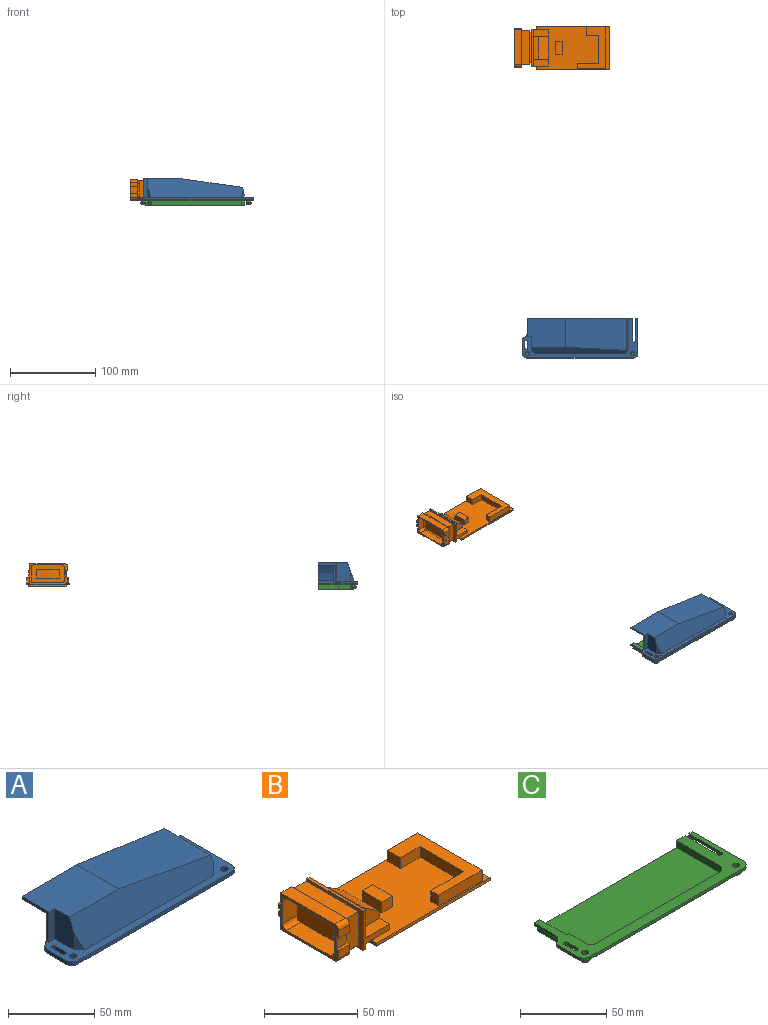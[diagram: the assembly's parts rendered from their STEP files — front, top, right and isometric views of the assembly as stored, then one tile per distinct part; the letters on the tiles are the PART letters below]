
ASSEMBLY  parts=3 mates=2
PART A: 68 faces, bbox 135.6x46.8x24 mm
  f0: plane 135.6x46.8mm, normal (0,0,1), area 1178.6mm2, adj f1,f4,f10,f13,f14,f29,f30,f31
  f1: plane 3x2.6mm, normal (0,1,0), area 7.8mm2, adj f0,f2,f56,f59
  f2: plane 135.6x46.8mm, normal (0,0,-1), area 690.3mm2, adj f1,f13,f14,f24,f25,f26,f27,f28
  f3: plane 119.6x44.8mm, normal (0,0,-1), area 500.9mm2, adj f5,f6,f13,f19,f20,f21,f22,f23
  f4: plane 21.4x15.83mm, normal (-1,0,0), area 320.8mm2, adj f0,f30,f33,f39,f44
  f5: plane 22x2.1mm, normal (0,1,0), area 45.5mm2, adj f3,f6,f9,f11,f12,f22,f40,f42
  f6: plane 21.5x20.4mm, normal (1,0,0), area 97.4mm2, adj f3,f5,f7,f9,f13,f46,f67
  f7: plane 16.1x1.8mm, normal (0,0,-1), area 28.9mm2, adj f6,f13,f43,f67
  f8: plane 20.1x2.9mm, normal (0,0,-1), area 58.4mm2, adj f10,f13,f43,f47,f66
  f9: plane 21.5x1.85mm, normal (0,0,-1), area 39.8mm2, adj f5,f6,f13,f40
  f10: plane 22x21.4mm, normal (-1,0,0), area 80.9mm2, adj f0,f8,f13,f33,f44,f66
  f11: plane 22x15.5mm, normal (1,0,0), area 314.3mm2, adj f5,f12,f18,f32,f38,f42,f48
  f12: plane 114x42mm, normal (0,0,-1), area 336.6mm2, adj f5,f11,f13,f15,f16,f17,f18,f19
  f13: plane 123.6x24mm, normal (0,1,0), area 271.4mm2, adj f0,f2,f3,f6,f7,f8,f9,f10
  f14: plane 125.6x2.6mm, normal (0,-1,0), area 326.6mm2, adj f0,f2,f54,f55
  f15: plane 37x2.88mm, normal (-1,0,0), area 106.6mm2, adj f12,f13,f16,f36
  f16: plane 7.91x3mm, normal (-0.71,0.71,0), area 22.5mm2, adj f12,f15,f17,f36,f38
  f17: plane 104x2.6mm, normal (0,1,0), area 270.4mm2, adj f12,f16,f18,f38
  f18: plane 10.84x3mm, normal (0.71,0.71,0), area 28.5mm2, adj f11,f12,f17,f38
  f19: plane 105.66x1.6mm, normal (0,-1,0), area 169.1mm2, adj f3,f12,f20,f23
  f20: plane 4.17x4.17mm, normal (0.71,-0.71,0), area 9.4mm2, adj f3,f12,f19,f21
  f21: plane 37.83x1.6mm, normal (1,0,0), area 60.5mm2, adj f3,f12,f13,f20
  f22: plane 16.33x1.6mm, normal (-1,0,0), area 26.1mm2, adj f3,f5,f12,f23
  f23: plane 4.17x4.17mm, normal (-0.71,-0.71,0), area 9.4mm2, adj f3,f12,f19,f22
  f24: plane 5.81x5.81mm, normal (0.71,0.71,0), area 13.2mm2, adj f2,f3,f25,f28
  f25: plane 18.89x1.6mm, normal (1,0,0), area 30.2mm2, adj f2,f3,f24,f47
  f26: plane 38.99x1.6mm, normal (-1,0,0), area 62.4mm2, adj f2,f3,f13,f27
  f27: plane 5.81x5.81mm, normal (-0.71,0.71,0), area 13.2mm2, adj f2,f3,f26,f28
  f28: plane 107.98x1.6mm, normal (0,1,0), area 172.8mm2, adj f2,f3,f24,f27
  f29: plane 37.83x0.01mm, normal (1,0,0), area 0.4mm2, adj f0,f13,f31,f37
  f30: plane 11.46x4.17mm, normal (-0.71,-0.71,0), area 33.8mm2, adj f0,f4,f39
  f31: plane 7.24x4.17mm, normal (0.71,-0.71,0), area 21.4mm2, adj f0,f29,f37,f39
  f32: plane 38x32.94mm, normal (0,0,-1), area 1212.6mm2, adj f11,f13,f34,f38,f41,f48,f49
  f33: plane 44.8x34.21mm, normal (0,0,1), area 1474mm2, adj f4,f10,f13,f35,f39,f44
  f34: plane 70.03x36.52mm, normal (-0.14,0,-0.99), area 2456mm2, adj f13,f32,f36,f38
  f35: plane 71.59x37.87mm, normal (0.14,0,0.99), area 2605.7mm2, adj f13,f33,f37,f39
  f36: plane 38.07x9.28mm, normal (-0.98,0,-0.21), area 354.9mm2, adj f13,f15,f16,f34,f38
  f37: plane 39.37x11.33mm, normal (0.98,0,0.21), area 447.1mm2, adj f13,f29,f31,f35,f39
  f38: plane 108.93x19.4mm, normal (0,0.94,-0.34), area 1852.1mm2, adj f11,f16,f17,f18,f32,f34,f36
  f39: plane 112.46x21.4mm, normal (0,-0.94,0.34), area 2131.1mm2, adj f0,f4,f30,f31,f33,f35,f37
  f40: plane 21.5x2mm, normal (-1,0,0), area 43mm2, adj f5,f9,f13,f42
  f41: plane 19.68x2mm, normal (1,0,0), area 39.4mm2, adj f13,f32,f42,f49
  f42: plane 23.5x2mm, normal (0,0,-1), area 44.4mm2, adj f5,f11,f13,f40,f41,f48,f49
  f43: plane 20.11x1.51mm, normal (-1,0,0), area 30.2mm2, adj f7,f8,f13,f45,f47
  f44: plane 21.4x4.8mm, normal (0,-1,0), area 102.7mm2, adj f0,f4,f10,f33
  f45: plane 18.91x4.01mm, normal (-1,0,0), area 38.7mm2, adj f3,f43,f46,f47,f67
  f46: plane 16.9x1.8mm, normal (0,1,0), area 30.4mm2, adj f3,f6,f45,f67
  f47: plane 22x2.9mm, normal (0,1,0), area 62.4mm2, adj f2,f3,f8,f25,f43,f45,f66
  f48: plane 2x0.29mm, normal (0.71,-0.71,0), area 0.8mm2, adj f11,f32,f42,f49
  f49: cylinder r=5mm len=3.54mm, axis (0,0,-1), area 7.9mm2, adj f32,f41,f42,f48
  f50: cylinder r=5mm len=2.6mm, axis (0,0,1), area 4.6mm2, adj f0,f2,f51,f66
  f51: plane 2.6x1mm, normal (-0.5,0.87,0), area 3mm2, adj f0,f2,f50,f52
  f52: cylinder r=5mm len=4.33mm, axis (0,0,1), area 13.6mm2, adj f0,f2,f51,f53
  f53: plane 15.11x2.6mm, normal (-1,0,0), area 39.3mm2, adj f0,f2,f52,f54
  f54: cylinder r=5mm len=5mm, axis (0,0,1), area 20.4mm2, adj f0,f2,f14,f53
  f55: cylinder r=5mm len=5mm, axis (0,0,1), area 20.4mm2, adj f0,f2,f14,f56
  f56: plane 41.8x2.6mm, normal (1,0,0), area 108.7mm2, adj f0,f1,f2,f55
  f57: cylinder r=2.25mm len=4.5mm, axis (0,0,1), area 36.8mm2, adj f0,f2
  f58: cylinder r=2.25mm len=4.5mm, axis (0,0,1), area 36.8mm2, adj f0,f2
  f59: plane 27x2.6mm, normal (-1,0,0), area 70.2mm2, adj f0,f1,f2,f60
  f60: cylinder r=1.5mm len=3mm, axis (0,0,-1), area 12.3mm2, adj f0,f2,f59,f61
  f61: plane 27x2.6mm, normal (1,0,0), area 70.2mm2, adj f0,f2,f13,f60
  f62: cylinder r=1.5mm len=3mm, axis (0,0,-1), area 12.3mm2, adj f0,f2,f63,f65
  f63: plane 8x2.6mm, normal (1,0,0), area 20.8mm2, adj f0,f2,f62,f64
  f64: cylinder r=1.5mm len=3mm, axis (0,0,-1), area 12.3mm2, adj f0,f2,f63,f65
  f65: plane 8x2.6mm, normal (-1,0,0), area 20.8mm2, adj f0,f2,f62,f64
  f66: cylinder r=1.5mm len=22mm, axis (0,0,1), area 3.5mm2, adj f0,f2,f8,f10,f47,f50
  f67: cylinder r=2mm len=2mm, axis (-1,0,0), area 5.6mm2, adj f6,f7,f45,f46
PART B: 97 faces, bbox 112.3x51x27.4 mm
  f0: plane 5x1.5mm, normal (1,0,0), area 7.5mm2, adj f7,f87,f89,f94
  f1: plane 78x2.4mm, normal (0,1,0), area 119.7mm2, adj f85,f88,f89,f94,f95,f96
  f2: plane 70x1.5mm, normal (0,-1,0), area 105mm2, adj f3,f85,f89,f94
  f3: plane 14x1.5mm, normal (1,0,0), area 21mm2, adj f2,f4,f89,f94
  f4: plane 70x1.5mm, normal (0,1,0), area 105mm2, adj f3,f86,f89,f94
  f5: plane 70x1.5mm, normal (0,-1,0), area 105mm2, adj f6,f86,f89,f94
  f6: plane 14x1.5mm, normal (1,0,0), area 21mm2, adj f5,f7,f89,f94
  f7: plane 70x1.5mm, normal (0,1,0), area 105mm2, adj f0,f6,f89,f94
  f8: plane 86x2mm, normal (0,1,0), area 172mm2, adj f15,f16,f17,f89
  f9: plane 86x2mm, normal (0,-1,0), area 172mm2, adj f15,f16,f17,f89
  f10: plane 8.3x8mm, normal (0,-1,0), area 66.4mm2, adj f61,f62,f75,f77
  f11: plane 8.3x8mm, normal (0,1,0), area 66.4mm2, adj f55,f61,f62,f72
  f12: plane 8.3x2mm, normal (0,1,0), area 16.6mm2, adj f61,f62,f71,f73
  f13: plane 43x8mm, normal (1,0,0), area 272mm2, adj f15,f33,f36,f37,f39,f40,f41,f42
  f14: plane 43x18.5mm, normal (1,0,0), area 444.5mm2, adj f33,f34,f36,f37,f38,f40,f41,f42
  f15: plane 86x51mm, normal (0,0,1), area 2972mm2, adj f8,f9,f13,f16,f17,f18,f19,f20
  f16: plane 51x2mm, normal (-1,0,0), area 102mm2, adj f8,f9,f15,f32,f89
  f17: plane 51x2mm, normal (1,0,0), area 102mm2, adj f8,f9,f15,f89
  f18: plane 33x7mm, normal (-1,0,0), area 231mm2, adj f15,f19,f25,f26
  f19: plane 15x7mm, normal (0,-1,0), area 105mm2, adj f15,f18,f20,f26
  f20: plane 10x7mm, normal (-1,0,0), area 70mm2, adj f15,f19,f21,f26
  f21: plane 23x7mm, normal (0,1,0), area 161mm2, adj f15,f20,f22,f26
  f22: plane 49x7mm, normal (1,0,0), area 343mm2, adj f15,f21,f23,f26
  f23: plane 33x7mm, normal (0,-1,0), area 231mm2, adj f15,f22,f24,f26
  f24: plane 7x6mm, normal (-1,0,0), area 42mm2, adj f15,f23,f25,f26
  f25: plane 25x7mm, normal (0,1,0), area 175mm2, adj f15,f18,f24,f26
  f26: plane 49x33mm, normal (0,0,1), area 692mm2, adj f18,f19,f20,f21,f22,f23,f24,f25
  f27: plane 8x7mm, normal (0,1,0), area 56mm2, adj f15,f28,f30,f31
  f28: plane 15x7mm, normal (1,0,0), area 105mm2, adj f15,f27,f29,f31
  f29: plane 8x7mm, normal (0,-1,0), area 56mm2, adj f15,f28,f30,f31
  f30: plane 15x7mm, normal (-1,0,0), area 105mm2, adj f15,f27,f29,f31
  f31: plane 15x8mm, normal (0,0,1), area 120mm2, adj f27,f28,f29,f30
  f32: plane 43x4.8mm, normal (0,0,-1), area 206.4mm2, adj f16,f36,f37,f44
  f33: plane 18.25x8mm, normal (0,0,1), area 146mm2, adj f13,f14,f36,f40
  f34: plane 43x1.75mm, normal (0,0,1), area 75.3mm2, adj f14,f35,f36,f37
  f35: plane 43x26mm, normal (-1,0,0), area 437.4mm2, adj f34,f36,f37,f43,f45,f46,f47,f48
  f36: plane 26x20mm, normal (0,1,0), area 107.2mm2, adj f13,f14,f15,f32,f33,f34,f35,f43
  f37: plane 26x20mm, normal (0,-1,0), area 107.2mm2, adj f13,f14,f15,f32,f34,f35,f41,f43
  f38: plane 27x6mm, normal (0,0,1), area 162mm2, adj f14,f39,f40,f42
  f39: plane 27x12.25mm, normal (0.57,0,0.82), area 402.6mm2, adj f13,f38,f40,f42
  f40: plane 18.25x13mm, normal (0,1,0), area 185.2mm2, adj f13,f14,f33,f38,f39
  f41: plane 18.25x8mm, normal (0,0,1), area 146mm2, adj f13,f14,f37,f42
  f42: plane 18.25x13mm, normal (0,-1,0), area 185.2mm2, adj f13,f14,f38,f39,f41
  f43: plane 43x1.2mm, normal (0,0,-1), area 51.6mm2, adj f35,f36,f37,f44
  f44: plane 43x4mm, normal (1,0,0), area 172mm2, adj f32,f36,f37,f43
  f45: plane 32x2mm, normal (0,0,1), area 64mm2, adj f35,f53,f90,f93
  f46: plane 15x2mm, normal (0,1,0), area 30mm2, adj f35,f53,f90,f91
  f47: plane 32x2mm, normal (0,0,-1), area 64mm2, adj f35,f53,f91,f92
  f48: plane 15x2mm, normal (0,-1,0), area 30mm2, adj f35,f53,f92,f93
  f49: plane 40x10mm, normal (0,0,1), area 400mm2, adj f50,f52,f53,f62
  f50: plane 22x10mm, normal (0,1,0), area 220mm2, adj f49,f51,f53,f62
  f51: plane 40x10mm, normal (0,0,-1), area 400mm2, adj f50,f52,f53,f62
  f52: plane 22x10mm, normal (0,-1,0), area 220mm2, adj f49,f51,f53,f62
  f53: plane 40x22mm, normal (1,0,0), area 199.4mm2, adj f45,f46,f47,f48,f49,f50,f51,f52
  f54: plane 8.3x8mm, normal (0,1,0), area 66.4mm2, adj f60,f61,f62,f69
  f55: plane 41x8.3mm, normal (0,0,-1), area 340.3mm2, adj f11,f61,f62,f79
  f56: plane 33x11mm, normal (0,0,-1), area 363mm2, adj f61,f63,f81,f84
  f57: plane 15x11mm, normal (0,1,0), area 165mm2, adj f61,f63,f81,f82
  f58: plane 33x11mm, normal (0,0,1), area 363mm2, adj f61,f63,f82,f83
  f59: plane 15x11mm, normal (0,-1,0), area 165mm2, adj f61,f63,f83,f84
  f60: plane 41x8.3mm, normal (0,0,1), area 340.3mm2, adj f54,f61,f62,f80
  f61: plane 46x24mm, normal (-1,0,0), area 236.9mm2, adj f10,f11,f12,f54,f55,f56,f57,f58
  f62: plane 46x24mm, normal (1,0,0), area 168.1mm2, adj f10,f11,f12,f49,f50,f51,f52,f54
  f63: plane 39x21mm, normal (-1,0,0), area 541.3mm2, adj f56,f57,f58,f59,f65,f66,f67,f68
  f64: plane 27x10mm, normal (-1,0,0), area 270mm2, adj f65,f66,f67,f68
  f65: plane 10x5.7mm, normal (0,-1,0), area 57mm2, adj f63,f64,f66,f68
  f66: plane 27x5.7mm, normal (0,0,1), area 153.9mm2, adj f63,f64,f65,f67
  f67: plane 10x5.7mm, normal (0,1,0), area 57mm2, adj f63,f64,f66,f68
  f68: plane 27x5.7mm, normal (0,0,-1), area 153.9mm2, adj f63,f64,f65,f67
  f69: plane 8.3x2mm, normal (0,0,1), area 16.6mm2, adj f54,f61,f62,f70
  f70: plane 8.3x3mm, normal (0,1,0), area 24.9mm2, adj f61,f62,f69,f71
  f71: plane 8.3x2mm, normal (0,0,-1), area 16.6mm2, adj f12,f61,f62,f70
  f72: plane 8.3x2mm, normal (0,0,-1), area 16.6mm2, adj f11,f61,f62,f74
  f73: plane 8.3x2mm, normal (0,0,1), area 16.6mm2, adj f12,f61,f62,f74
  f74: plane 8.3x3mm, normal (0,1,0), area 24.9mm2, adj f61,f62,f72,f73
  f75: plane 8.3x2mm, normal (0,0,-1), area 16.6mm2, adj f10,f61,f62,f76
  f76: plane 8.3x5mm, normal (0,-1,0), area 41.5mm2, adj f61,f62,f75,f80
  f77: plane 8.3x2mm, normal (0,0,1), area 16.6mm2, adj f10,f61,f62,f78
  f78: plane 8.3x5mm, normal (0,-1,0), area 41.5mm2, adj f61,f62,f77,f79
  f79: cylinder r=3mm len=8.3mm, axis (-1,0,0), area 39.1mm2, adj f55,f61,f62,f78
  f80: cylinder r=3mm len=8.3mm, axis (-1,0,0), area 39.1mm2, adj f60,f61,f62,f76
  f81: cylinder r=3mm len=11mm, axis (-1,0,0), area 51.8mm2, adj f56,f57,f61,f63
  f82: cylinder r=3mm len=11mm, axis (1,0,0), area 51.8mm2, adj f57,f58,f61,f63
  f83: cylinder r=3mm len=11mm, axis (-1,0,0), area 51.8mm2, adj f58,f59,f61,f63
  f84: cylinder r=3mm len=11mm, axis (1,0,0), area 51.8mm2, adj f56,f59,f61,f63
  f85: plane 5x1.5mm, normal (1,0,0), area 7.5mm2, adj f1,f2,f89,f94
  f86: plane 7x1.5mm, normal (1,0,0), area 10.5mm2, adj f4,f5,f89,f94
  f87: plane 78x2.4mm, normal (0,-1,0), area 119.7mm2, adj f0,f88,f89,f94,f95,f96
  f88: plane 45x2.4mm, normal (-1,0,0), area 108mm2, adj f1,f87,f89,f95
  f89: plane 86x51mm, normal (0,0,-1), area 2836mm2, adj f0,f1,f2,f3,f4,f5,f6,f7
  f90: cylinder r=2mm len=2mm, axis (-1,0,0), area 6.3mm2, adj f35,f45,f46,f53
  f91: cylinder r=2mm len=2mm, axis (1,0,0), area 6.3mm2, adj f35,f46,f47,f53
  f92: cylinder r=2mm len=2mm, axis (-1,0,0), area 6.3mm2, adj f35,f47,f48,f53
  f93: cylinder r=2mm len=2mm, axis (1,0,0), area 6.3mm2, adj f35,f45,f48,f53
  f94: plane 75x45mm, normal (0,0,-1), area 1415mm2, adj f0,f1,f2,f3,f4,f5,f6,f7
  f95: plane 45x3mm, normal (0,0,-1), area 135mm2, adj f1,f87,f88,f96
  f96: plane 45x0.9mm, normal (1,0,0), area 40.5mm2, adj f1,f87,f94,f95
PART C: 46 faces, bbox 135.6x46.8x7 mm
  f0: plane 135.6x46.8mm, normal (0,0,-1), area 1213.2mm2, adj f2,f3,f4,f5,f13,f14,f15,f16
  f1: plane 135.6x46.8mm, normal (0,0,1), area 1628.2mm2, adj f2,f3,f4,f5,f6,f7,f8,f9
  f2: plane 3x2mm, normal (0,1,0), area 6mm2, adj f0,f1,f23,f27
  f3: plane 17.45x2mm, normal (-1,0,0), area 34.9mm2, adj f0,f1,f4,f32
  f4: plane 123.6x7mm, normal (0,1,0), area 267.2mm2, adj f0,f1,f3,f10,f12,f13,f14,f20
  f5: plane 125.6x2mm, normal (0,-1,0), area 251.2mm2, adj f0,f1,f33,f35
  f6: plane 15.5x5mm, normal (1,0,0), area 77.5mm2, adj f1,f7,f11,f20
  f7: plane 5x3mm, normal (0.71,0.71,0), area 21.2mm2, adj f1,f6,f8,f20
  f8: plane 104x5mm, normal (0,1,0), area 520mm2, adj f1,f7,f9,f20
  f9: plane 5x3mm, normal (-0.71,0.71,0), area 21.2mm2, adj f1,f8,f10,f20
  f10: plane 37x5mm, normal (-1,0,0), area 185mm2, adj f1,f4,f9,f20
  f11: plane 5x2mm, normal (0,1,0), area 10mm2, adj f1,f6,f12,f20
  f12: plane 21.5x5mm, normal (1,0,0), area 107.5mm2, adj f1,f4,f11,f20
  f13: plane 23.5x5mm, normal (-1,0,0), area 117.5mm2, adj f0,f4,f19,f21
  f14: plane 37.83x5mm, normal (1,0,0), area 189.1mm2, adj f0,f4,f15,f21
  f15: plane 5x4.17mm, normal (0.71,-0.71,0), area 29.5mm2, adj f0,f14,f16,f21
  f16: plane 105.66x5mm, normal (0,-1,0), area 528.3mm2, adj f0,f15,f17,f21
  f17: plane 5x4.17mm, normal (-0.71,-0.71,0), area 29.5mm2, adj f0,f16,f18,f21
  f18: plane 14.33x5mm, normal (-1,0,0), area 71.6mm2, adj f0,f17,f19,f21
  f19: plane 5x2mm, normal (0,-1,0), area 10mm2, adj f0,f13,f18,f21
  f20: plane 112x40mm, normal (0,0,1), area 4434mm2, adj f4,f6,f7,f8,f9,f10,f11,f12
  f21: plane 116x42mm, normal (0,0,-1), area 4817.6mm2, adj f4,f13,f14,f15,f16,f17,f18,f19
  f22: plane 15.11x2mm, normal (-1,0,0), area 30.2mm2, adj f0,f1,f33,f34
  f23: plane 41.8x2mm, normal (1,0,0), area 83.6mm2, adj f0,f1,f2,f35
  f24: plane 8x2mm, normal (-1,0,0), area 16mm2, adj f0,f1,f28,f29
  f25: plane 8x2mm, normal (1,0,0), area 16mm2, adj f0,f1,f28,f29
  f26: plane 27x2mm, normal (1,0,0), area 54mm2, adj f0,f1,f4,f30
  f27: plane 27x2mm, normal (-1,0,0), area 54mm2, adj f0,f1,f2,f30
  f28: cylinder r=1.5mm len=3mm, axis (0,0,1), area 9.4mm2, adj f0,f1,f24,f25
  f29: cylinder r=1.5mm len=3mm, axis (0,0,1), area 9.4mm2, adj f0,f1,f24,f25
  f30: cylinder r=1.5mm len=3mm, axis (0,0,-1), area 9.4mm2, adj f0,f1,f26,f27
  f31: plane 2x1mm, normal (-0.5,0.87,0), area 2.3mm2, adj f0,f1,f32,f34
  f32: cylinder r=5mm len=4.33mm, axis (0,0,-1), area 10.5mm2, adj f0,f1,f3,f31
  f33: cylinder r=5mm len=5mm, axis (0,0,1), area 15.7mm2, adj f0,f1,f5,f22
  f34: cylinder r=5mm len=4.33mm, axis (0,0,1), area 10.5mm2, adj f0,f1,f22,f31
  f35: cylinder r=5mm len=5mm, axis (0,0,-1), area 15.7mm2, adj f0,f1,f5,f23
  f36: cylinder r=2mm len=5mm, axis (0,0,1), area 62.8mm2, adj f1,f42
  f37: cylinder r=2mm len=5mm, axis (0,0,1), area 62.8mm2, adj f1,f43
  f38: cylinder r=3mm len=6mm, axis (0,0,1), area 37.7mm2, adj f0,f45
  f39: plane 2x2mm, normal (0,0,-1), area 3.1mm2, adj f45
  f40: cylinder r=3mm len=6mm, axis (0,0,1), area 37.7mm2, adj f0,f44
  f41: plane 2x2mm, normal (0,0,-1), area 3.1mm2, adj f44
  f42: plane 4x4mm, normal (0,0,1), area 12.6mm2, adj f36
  f43: plane 4x4mm, normal (0,0,1), area 12.6mm2, adj f37
  f44: torus R=1mm, axis (0,0,-1), area 44.9mm2, adj f40,f41
  f45: torus R=1mm, axis (0,0,-1), area 44.9mm2, adj f38,f39
PLACE A t=(-80.08,-338.74,79.19)mm
PLACE B t=(-88.08,-21.1,72.64)mm fixed
PLACE C t=(-80.08,-338.74,79.19)mm
MATE slider A.f58 <-> C.f37  axis (0,0,-1) through (-141.88,-380.54,77.59)mm
MATE slider B.f48 <-> A.f46  axis (0,-1,0) through (-138.08,-39.1,88.64)mm
